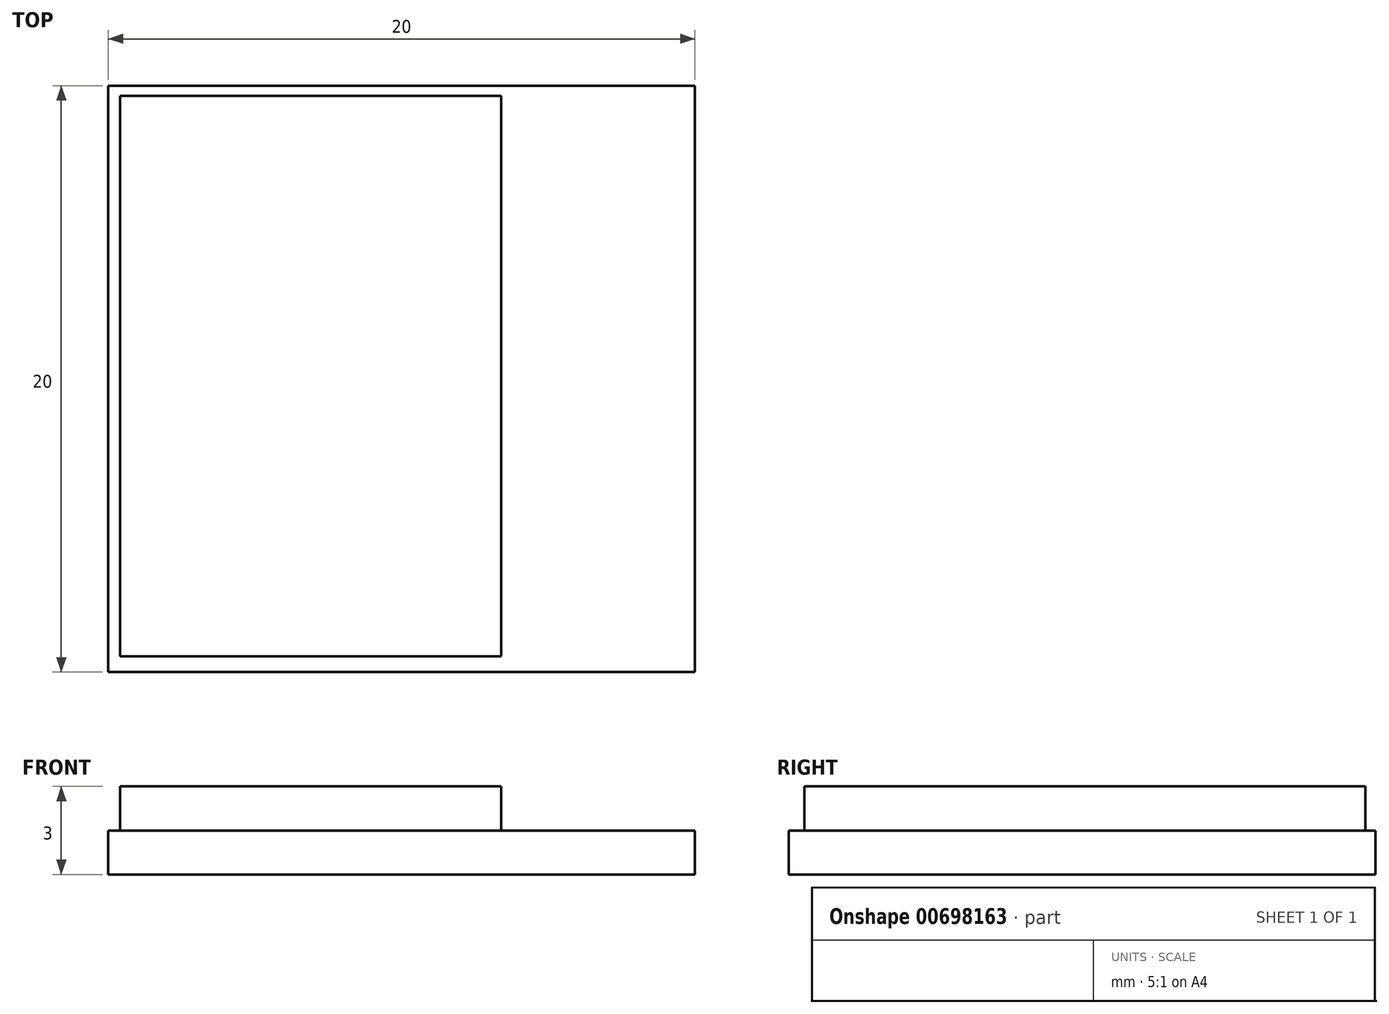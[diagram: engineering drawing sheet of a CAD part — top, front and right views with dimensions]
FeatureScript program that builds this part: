
annotation { "Feature Type Name" : "Feature", "Feature Type Description" : "" }
export const myFeature = defineFeature(function(context is Context, id is Id, definition is map)
    precondition{}
    {
        {
            var Q0;
            Q0=qCreatedBy(makeId("Top.planeOp"),FACE);
            var sketch = newSketch(context, id + "F0", { "sketchPlane" : qUnion([Q0])});
            skLineSegment(sketch, "E0.bottom", {"start": v(10, 10) * mm, "end": v(-10, 10) * mm});
            skLineSegment(sketch, "E0.top", {"start": v(10, -10) * mm, "end": v(-10, -10) * mm});
            skLineSegment(sketch, "E0.left", {"start": v(10, 10) * mm, "end": v(10, -10) * mm});
            skLineSegment(sketch, "E0.right", {"start": v(-10, 10) * mm, "end": v(-10, -10) * mm});
            skPoint(sketch, "E0.middle", {"position": v(0, 0) * mm});
            skSolve(sketch);
        }
        {
            var Q0;
            Q0=makeQuery(id+"F0.imprint","IMPRINT",FACE,{"disambiguationData":[TD([[makeQuery(id+"F0.imprint","IMPRINT",EDGE,{"derivedFrom":sQuery(id+"F0.wireOp",EDGE,"E0.bottom")}),1.0]])]});
            extrude(context, id + "F1", {"entities" : qUnion([Q0]), "depth" : 1.5 * mm, "offsetDistance" : 25 * mm});
        }
        {
            var Q0;
            Q0=qCreatedBy(makeId("Top.planeOp"),FACE);
            cPlane(context, id + "F2", {"entities" : qUnion([Q0]), "cplaneType" : CPlaneType.OFFSET, "offset" : 1.5 * mm, "width" : 150 * mm, "height" : 150 * mm});
        }
        {
            var Q0;
            Q0=qCreatedBy(id+"F2.planeOp",FACE);
            var sketch = newSketch(context, id + "F3", { "sketchPlane" : qUnion([Q0])});
            skLineSegment(sketch, "E1.bottom", {"start": v(-9.6, -9.47) * mm, "end": v(3.4, -9.47) * mm});
            skLineSegment(sketch, "E1.top", {"start": v(-9.6, 9.66) * mm, "end": v(3.4, 9.66) * mm});
            skLineSegment(sketch, "E1.left", {"start": v(-9.6, -9.47) * mm, "end": v(-9.6, 9.66) * mm});
            skLineSegment(sketch, "E1.right", {"start": v(3.4, -9.47) * mm, "end": v(3.4, 9.66) * mm});
            skSolve(sketch);
        }
        {
            var Q0;
            Q0 = qSketchRegion(id + "F3", true);
            extrude(context, id + "F4", {"entities" : qUnion([Q0]), "operationType" : NewBodyOperationType.ADD, "depth" : 1.5 * mm, "offsetDistance" : 25 * mm});
        }
    });
